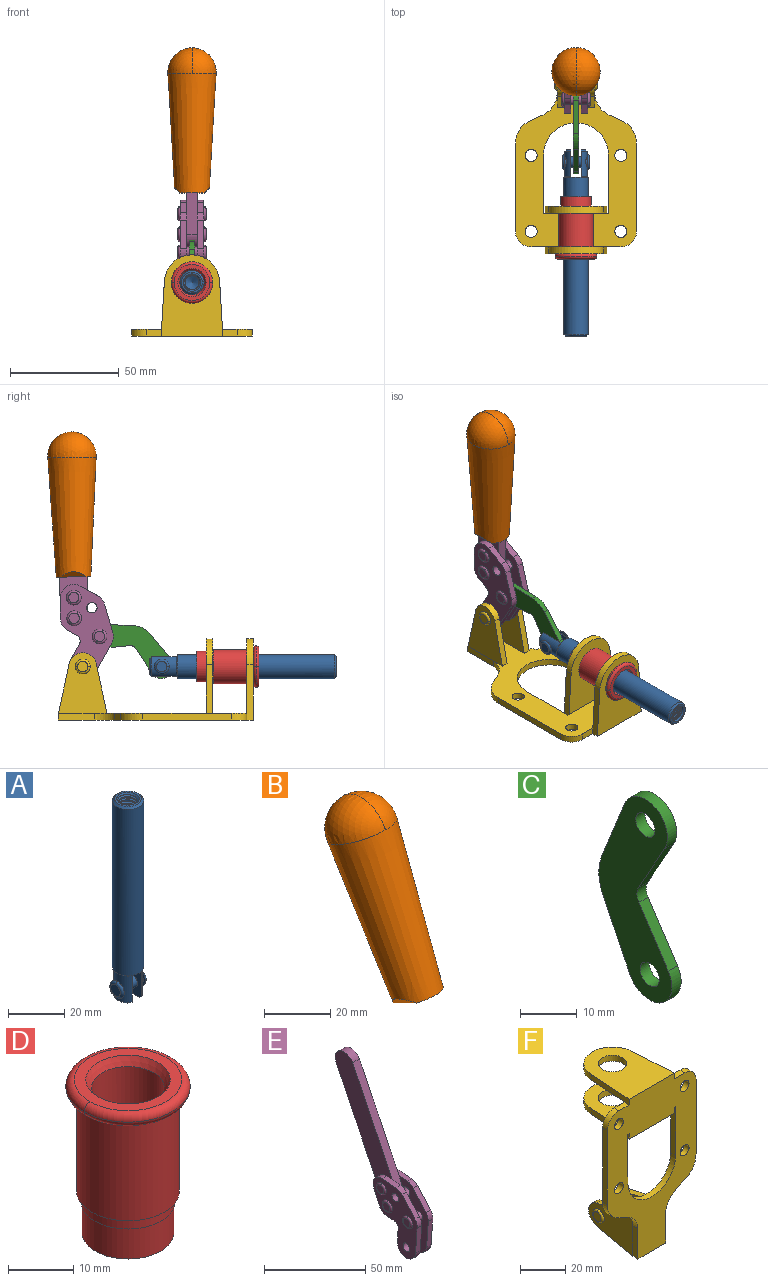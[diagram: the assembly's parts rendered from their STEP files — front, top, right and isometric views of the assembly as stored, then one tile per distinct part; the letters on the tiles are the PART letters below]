
ASSEMBLY  parts=6 mates=6
PART A: 48 faces, bbox 12.6x11.1x86.1 mm
  f0: torus R=2.41mm, axis (-1,0,0), area 15mm2, adj f30,f32,f34
  f1: torus R=2.41mm, axis (-1,0,0), area 15mm2, adj f29,f31,f33
  f2: cylinder r=5.54mm len=72.39mm, axis (0,0,1), area 2518.5mm2, adj f3,f4,f42,f43
  f3: cone r=5.54mm half-angle=45deg, axis (0,0,1), area 7.6mm2, adj f2,f5,f41
  f4: cone r=5.54mm half-angle=45deg, axis (0,0,-1), area 34.9mm2, adj f2,f39
  f5: cylinder r=5.08mm len=11.48mm, axis (0,0,1), area 108.3mm2, adj f3,f7,f8,f41
  f6: cylinder r=2.41mm len=4.83mm, axis (-1,0,0), area 71.2mm2, adj f40,f41
  f7: cylinder r=2.41mm len=4.83mm, axis (-1,0,0), area 7.6mm2, adj f5,f34
  f8: cone r=5.08mm half-angle=45deg, axis (0,0,1), area 10.6mm2, adj f5,f37,f41
  f9: cone r=3.98mm half-angle=45deg, axis (0,0,1), area 17.6mm2, adj f27,f39,f45,f46,f47
  f10: cylinder r=2.41mm len=4.83mm, axis (-1,0,0), area 7.6mm2, adj f33,f38
  f11: cylinder r=3.2mm len=6.4mm, axis (0,0,1), area 78.4mm2, adj f12,f28,f44,f45,f47
  f12: cylinder r=3.2mm len=6.4mm, axis (0,0,1), area 10.5mm2, adj f11,f13,f45,f47
  f13: cylinder r=3.2mm len=6.4mm, axis (0,0,1), area 10.5mm2, adj f12,f14,f45,f47
  f14: cylinder r=3.2mm len=6.4mm, axis (0,0,1), area 10.5mm2, adj f13,f15,f45,f47
  f15: cylinder r=3.2mm len=6.4mm, axis (0,0,1), area 10.5mm2, adj f14,f16,f45,f47
  f16: cylinder r=3.2mm len=6.4mm, axis (0,0,1), area 10.5mm2, adj f15,f17,f45,f47
  f17: cylinder r=3.2mm len=6.4mm, axis (0,0,1), area 10.5mm2, adj f16,f18,f45,f47
  f18: cylinder r=3.2mm len=6.4mm, axis (0,0,1), area 10.5mm2, adj f17,f19,f45,f47
  f19: cylinder r=3.2mm len=6.4mm, axis (0,0,1), area 10.5mm2, adj f18,f20,f45,f47
  f20: cylinder r=3.2mm len=6.4mm, axis (0,0,1), area 10.5mm2, adj f19,f21,f45,f47
  f21: cylinder r=3.2mm len=6.4mm, axis (0,0,1), area 10.5mm2, adj f20,f22,f45,f47
  f22: cylinder r=3.2mm len=6.4mm, axis (0,0,1), area 10.5mm2, adj f21,f23,f45,f47
  f23: cylinder r=3.2mm len=6.4mm, axis (0,0,1), area 10.5mm2, adj f22,f24,f45,f47
  f24: cylinder r=3.2mm len=6.4mm, axis (0,0,1), area 10.5mm2, adj f23,f25,f45,f47
  f25: cylinder r=3.2mm len=6.4mm, axis (0,0,1), area 10.5mm2, adj f24,f26,f45,f47
  f26: cylinder r=3.2mm len=6.4mm, axis (0,0,1), area 10.5mm2, adj f25,f27,f45,f47
  f27: cylinder r=3.2mm len=6.4mm, axis (0,0,1), area 7.4mm2, adj f9,f26,f45,f47
  f28: cone r=3.2mm half-angle=60deg, axis (0,0,1), area 37.2mm2, adj f11
  f29: plane 4.83x4.83mm, normal (-1,0,0), area 18.3mm2, adj f1,f31
  f30: plane 4.83x4.83mm, normal (1,0,0), area 18.3mm2, adj f0,f32
  f31: torus R=2.41mm, axis (-1,0,0), area 15mm2, adj f1,f29,f33
  f32: torus R=2.41mm, axis (-1,0,0), area 15mm2, adj f0,f30,f34
  f33: plane 6.83x6.83mm, normal (1,0,0), area 18.3mm2, adj f1,f10,f31
  f34: plane 6.83x6.83mm, normal (-1,0,0), area 18.3mm2, adj f0,f7,f32
  f35: cone r=5.08mm half-angle=45deg, axis (0,0,1), area 10.6mm2, adj f36,f38,f40
  f36: plane 7.25x1.97mm, normal (0,0,-1), area 10mm2, adj f35,f40
  f37: plane 7.25x1.97mm, normal (0,0,-1), area 10mm2, adj f8,f41
  f38: cylinder r=5.08mm len=11.48mm, axis (0,0,1), area 108.3mm2, adj f10,f35,f40,f42
  f39: plane 9.55x9.55mm, normal (0,0,1), area 22mm2, adj f4,f9
  f40: plane 12.76x10.09mm, normal (1,0,0), area 95.7mm2, adj f6,f35,f36,f38,f42,f43
  f41: plane 12.76x10.09mm, normal (-1,0,0), area 95.7mm2, adj f3,f5,f6,f8,f37,f43
  f42: cone r=5.54mm half-angle=45deg, axis (0,0,1), area 7.6mm2, adj f2,f38,f40
  f43: plane 11.07x4.7mm, normal (0,0,-1), area 50.4mm2, adj f2,f40,f41
  f44: plane 0.89x0.62mm, normal (-1,0,0), area 0.3mm2, adj f11,f45,f46,f47
  f45: bspline ~24.8x7.63mm, area 266.6mm2, adj f9,f11,f12,f13,f14,f15,f16,f17
  f46: bspline ~24.87x7.63mm, area 73.6mm2, adj f9,f44,f45,f47
  f47: bspline ~24.98x7.63mm, area 272.5mm2, adj f9,f11,f12,f13,f14,f15,f16,f17
PART B: 11 faces, bbox 22.3x42.6x64.5 mm
  f0: sphere r=11.13mm, area 411.4mm2, adj f1,f8
  f1: cone r=11.11mm half-angle=3.3deg, axis (0,0.44,0.9), area 3251.8mm2, adj f0,f7,f8,f9,f10
  f2: cylinder r=6.16mm len=11.7mm, axis (1,0,0), area 89.5mm2, adj f3,f4,f5,f6
  f3: plane 60.23x36.75mm, normal (-1,0,0), area 763.6mm2, adj f2,f4,f6,f10
  f4: plane 51.37x25.05mm, normal (0,0.9,-0.44), area 264.2mm2, adj f2,f3,f5,f10
  f5: plane 60.23x36.75mm, normal (1,0,0), area 763.6mm2, adj f2,f4,f6,f10
  f6: plane 51.37x25.05mm, normal (0,-0.9,0.44), area 264.2mm2, adj f2,f3,f5,f10
  f7: plane 9.95x5.95mm, normal (0.71,-0.31,-0.64), area 25.8mm2, adj f1,f10
  f8: sphere r=11.13mm, area 411.4mm2, adj f0,f1
  f9: plane 9.95x5.95mm, normal (-0.71,-0.31,-0.64), area 25.8mm2, adj f1,f10
  f10: plane 14.27x11.38mm, normal (0,-0.44,-0.9), area 106.7mm2, adj f1,f3,f4,f5,f6,f7,f9
PART C: 12 faces, bbox 2.3x18.2x42.8 mm
  f0: cylinder r=2.4mm len=4.8mm, axis (1,0,0), area 34.9mm2, adj f4,f11
  f1: cylinder r=10.41mm len=8.47mm, axis (1,0,0), area 20.2mm2, adj f4,f9,f10,f11
  f2: cylinder r=3.05mm len=3.16mm, axis (1,0,0), area 7.7mm2, adj f4,f6,f7,f11
  f3: cylinder r=2.4mm len=4.8mm, axis (1,0,0), area 34.9mm2, adj f4,f11
  f4: plane 42.81x18.23mm, normal (-1,0,0), area 414.1mm2, adj f0,f1,f2,f3,f5,f6,f7,f8
  f5: cylinder r=5.54mm len=10.67mm, axis (1,0,0), area 41.8mm2, adj f4,f6,f10,f11
  f6: plane 11.66x6.53mm, normal (0,-0.87,-0.49), area 30.9mm2, adj f2,f4,f5,f11
  f7: plane 11.17x7.33mm, normal (0,-0.84,0.55), area 30.9mm2, adj f2,f4,f8,f11
  f8: cylinder r=5.54mm len=10.51mm, axis (1,0,0), area 41.8mm2, adj f4,f7,f9,f11
  f9: plane 13.67x6.67mm, normal (0,0.9,-0.44), area 35.1mm2, adj f1,f4,f8,f11
  f10: plane 14.1x5.7mm, normal (0,0.93,0.37), area 35.1mm2, adj f1,f4,f5,f11
  f11: plane 42.81x18.23mm, normal (1,0,0), area 414.1mm2, adj f0,f1,f2,f3,f5,f6,f7,f8
PART D: 15 faces, bbox 20.6x20.6x28.7 mm
  f0: torus R=8.26mm, axis (0,0,1), area 56.8mm2, adj f1,f10,f12
  f1: torus R=8.26mm, axis (0,0,1), area 56.8mm2, adj f0,f6,f13
  f2: cylinder r=5.59mm len=25.91mm, axis (0,0,1), area 909.6mm2, adj f3,f4
  f3: cone r=6.86mm half-angle=45deg, axis (0,0,-1), area 70.2mm2, adj f2,f14
  f4: cone r=6.47mm half-angle=30deg, axis (0,0,1), area 66.7mm2, adj f2,f13
  f5: cylinder r=7.04mm len=14.07mm, axis (0,0,1), area 252.6mm2, adj f11,f14
  f6: torus R=8.26mm, axis (0,0,1), area 56.8mm2, adj f1,f12,f13
  f7: cylinder r=7.16mm len=14.33mm, axis (0,0,1), area 91.5mm2, adj f9,f11
  f8: cylinder r=7.86mm len=18.42mm, axis (0,0,1), area 909.6mm2, adj f9,f10
  f9: plane 15.72x15.72mm, normal (0,0,-1), area 33mm2, adj f7,f8
  f10: plane 16.51x16.51mm, normal (0,0,-1), area 19.9mm2, adj f0,f8,f12
  f11: plane 14.33x14.33mm, normal (0,0,-1), area 5.7mm2, adj f5,f7
  f12: torus R=8.26mm, axis (0,0,1), area 56.8mm2, adj f0,f6,f10
  f13: plane 16.51x16.51mm, normal (0,0,1), area 82.7mm2, adj f1,f4,f6
  f14: plane 14.07x14.07mm, normal (0,0,-1), area 7.8mm2, adj f3,f5
PART E: 59 faces, bbox 12.9x60.2x99.6 mm
  f0: torus R=2.39mm, axis (-1,0,0), area 14.9mm2, adj f20,f43,f51
  f1: torus R=2.39mm, axis (-1,0,0), area 14.9mm2, adj f19,f42,f51
  f2: torus R=2.39mm, axis (-1,0,0), area 14.9mm2, adj f18,f35,f51
  f3: torus R=2.39mm, axis (-1,0,0), area 14.9mm2, adj f14,f17,f23
  f4: torus R=2.39mm, axis (-1,0,0), area 14.9mm2, adj f13,f16,f23
  f5: torus R=2.39mm, axis (-1,0,0), area 14.9mm2, adj f12,f15,f23
  f6: cylinder r=2.39mm len=4.78mm, axis (1,0,0), area 46.5mm2, adj f48,f50,f51
  f7: cylinder r=2.39mm len=4.78mm, axis (1,0,0), area 46.5mm2, adj f50,f51
  f8: cylinder r=6.35mm len=12.68mm, axis (1,0,0), area 61.8mm2, adj f38,f39,f50,f51
  f9: cylinder r=2.39mm len=4.78mm, axis (-1,0,0), area 70.5mm2, adj f46,f50
  f10: cylinder r=2.39mm len=4.78mm, axis (-1,0,0), area 46.5mm2, adj f23,f45,f46
  f11: cylinder r=2.39mm len=4.78mm, axis (-1,0,0), area 46.5mm2, adj f23,f46
  f12: plane 4.78x4.78mm, normal (1,0,0), area 17.9mm2, adj f5,f15
  f13: plane 4.78x4.78mm, normal (1,0,0), area 17.9mm2, adj f4,f16
  f14: plane 4.78x4.78mm, normal (1,0,0), area 17.9mm2, adj f3,f17
  f15: torus R=2.39mm, axis (-1,0,0), area 14.9mm2, adj f5,f12,f23
  f16: torus R=2.39mm, axis (-1,0,0), area 14.9mm2, adj f4,f13,f23
  f17: torus R=2.39mm, axis (-1,0,0), area 14.9mm2, adj f3,f14,f23
  f18: plane 4.78x4.78mm, normal (-1,0,0), area 17.9mm2, adj f2,f35
  f19: plane 4.78x4.78mm, normal (-1,0,0), area 17.9mm2, adj f1,f42
  f20: plane 4.78x4.78mm, normal (-1,0,0), area 17.9mm2, adj f0,f43
  f21: plane 2.26x0.2mm, normal (1,0,0), area 0.2mm2, adj f31,f44
  f22: plane 2.26x0.2mm, normal (-1,0,0), area 0.2mm2, adj f41,f44
  f23: plane 39.37x30.77mm, normal (1,0,0), area 565.5mm2, adj f3,f4,f5,f10,f11,f15,f16,f17
  f24: cylinder r=6.1mm len=4.15mm, axis (-1,0,0), area 14.7mm2, adj f23,f25,f32,f46
  f25: plane 10.25x9.01mm, normal (0,-0.75,0.66), area 42.3mm2, adj f23,f24,f26,f46
  f26: cylinder r=6.35mm len=4.64mm, axis (-1,0,0), area 15.6mm2, adj f23,f25,f27,f46
  f27: plane 15.84x3.1mm, normal (0,-1,-0.07), area 49.2mm2, adj f23,f26,f28,f46
  f28: cylinder r=6.35mm len=12.68mm, axis (-1,0,0), area 61.8mm2, adj f23,f27,f29,f46
  f29: plane 8.11x3.1mm, normal (0,1,0.07), area 25.2mm2, adj f23,f28,f30,f46
  f30: cylinder r=3.05mm len=3.25mm, axis (-1,0,0), area 14.8mm2, adj f23,f29,f31,f46
  f31: plane 5.99x3.1mm, normal (0,0.07,-1), area 18.6mm2, adj f21,f23,f30,f44,f46
  f32: plane 9.5x3.1mm, normal (0,-0.07,1), area 29.5mm2, adj f23,f24,f33,f46,f47
  f33: cylinder r=6.1mm len=8.63mm, axis (-1,0,0), area 39.1mm2, adj f23,f32,f34,f47
  f34: plane 8.65x3.96mm, normal (0,0.91,-0.42), area 29.5mm2, adj f23,f33,f44,f47
  f35: torus R=2.39mm, axis (-1,0,0), area 14.9mm2, adj f2,f18,f51
  f36: plane 10.25x9.01mm, normal (0,-0.75,0.66), area 42.3mm2, adj f37,f49,f50,f51
  f37: cylinder r=6.35mm len=4.64mm, axis (1,0,0), area 15.6mm2, adj f36,f38,f50,f51
  f38: plane 15.84x3.1mm, normal (0,-1,-0.07), area 49.2mm2, adj f8,f37,f50,f51
  f39: plane 8.11x3.1mm, normal (0,1,0.07), area 25.2mm2, adj f8,f40,f50,f51
  f40: cylinder r=3.05mm len=3.25mm, axis (1,0,0), area 14.8mm2, adj f39,f41,f50,f51
  f41: plane 5.99x3.1mm, normal (0,0.07,-1), area 18.6mm2, adj f22,f40,f44,f50,f51
  f42: torus R=2.39mm, axis (-1,0,0), area 14.9mm2, adj f1,f19,f51
  f43: torus R=2.39mm, axis (-1,0,0), area 14.9mm2, adj f0,f20,f51
  f44: cylinder r=6.35mm len=12.12mm, axis (-1,0,0), area 128.9mm2, adj f21,f22,f23,f31,f34,f41,f46,f47
  f45: plane 2.65x1.35mm, normal (1,0,0), area 1mm2, adj f10,f55
  f46: plane 39.08x20.42mm, normal (-1,0,0), area 412.5mm2, adj f9,f10,f11,f24,f25,f26,f27,f28
  f47: plane 77.62x39.82mm, normal (1,0,0), area 850mm2, adj f32,f33,f34,f44,f53,f54,f55
  f48: plane 2.65x1.35mm, normal (-1,0,0), area 1mm2, adj f6,f55
  f49: cylinder r=6.1mm len=4.15mm, axis (1,0,0), area 14.7mm2, adj f36,f50,f51,f56
  f50: plane 39.08x20.42mm, normal (1,0,0), area 412.5mm2, adj f6,f7,f8,f9,f36,f37,f38,f39
  f51: plane 39.37x30.77mm, normal (-1,0,0), area 565.5mm2, adj f0,f1,f2,f6,f7,f8,f35,f36
  f52: plane 8.65x3.96mm, normal (0,0.91,-0.42), area 29.5mm2, adj f44,f51,f57,f58
  f53: plane 68.49x33.4mm, normal (0,0.9,-0.44), area 358.1mm2, adj f44,f47,f54,f58
  f54: cylinder r=6.35mm len=12.06mm, axis (1,0,0), area 93.7mm2, adj f47,f53,f55,f58
  f55: plane 68.49x33.4mm, normal (0,-0.9,0.44), area 358.1mm2, adj f44,f45,f46,f47,f48,f50,f54,f58
  f56: plane 9.5x3.1mm, normal (0,-0.07,1), area 29.5mm2, adj f49,f50,f51,f57,f58
  f57: cylinder r=6.1mm len=8.63mm, axis (1,0,0), area 39.1mm2, adj f51,f52,f56,f58
  f58: plane 77.62x39.82mm, normal (-1,0,0), area 850mm2, adj f44,f52,f53,f54,f55,f56,f57
PART F: 55 faces, bbox 55.7x37.4x89.8 mm
  f0: torus R=2.41mm, axis (-1,0,0), area 15mm2, adj f11,f15,f25
  f1: torus R=2.41mm, axis (-1,0,0), area 15mm2, adj f10,f12,f22
  f2: cylinder r=2.78mm len=5.56mm, axis (0,-1,0), area 54.2mm2, adj f30,f54
  f3: cylinder r=14.99mm len=29.97mm, axis (0,-1,0), area 145.9mm2, adj f30,f49,f53,f54
  f4: cylinder r=2.78mm len=5.56mm, axis (0,-1,0), area 54.2mm2, adj f30,f54
  f5: cylinder r=2.78mm len=5.56mm, axis (0,-1,0), area 54.2mm2, adj f30,f54
  f6: cylinder r=2.78mm len=5.56mm, axis (0,-1,0), area 54.2mm2, adj f30,f54
  f7: cylinder r=6.35mm len=12.7mm, axis (0,0,1), area 123.6mm2, adj f27,f51
  f8: cylinder r=6.35mm len=12.7mm, axis (0,0,-1), area 124.7mm2, adj f21,f35
  f9: cylinder r=2.41mm len=11.18mm, axis (-1,0,0), area 169.4mm2, adj f16,f19
  f10: plane 4.83x4.83mm, normal (1,0,0), area 18.3mm2, adj f1,f12
  f11: plane 4.83x4.83mm, normal (-1,0,0), area 18.3mm2, adj f0,f15
  f12: torus R=2.41mm, axis (-1,0,0), area 15mm2, adj f1,f10,f22
  f13: cylinder r=6.35mm len=12.41mm, axis (1,0,0), area 53.4mm2, adj f18,f19,f22,f23
  f14: cylinder r=6.35mm len=12.41mm, axis (-1,0,0), area 53.4mm2, adj f16,f17,f24,f25
  f15: torus R=2.41mm, axis (-1,0,0), area 15mm2, adj f0,f11,f25
  f16: plane 27.86x22.35mm, normal (1,0,0), area 425.4mm2, adj f9,f14,f17,f24,f30
  f17: plane 22.86x4.97mm, normal (0,0.21,0.98), area 72.5mm2, adj f14,f16,f25,f30
  f18: plane 22.86x4.97mm, normal (0,0.21,0.98), area 72.5mm2, adj f13,f19,f22,f30
  f19: plane 27.86x22.35mm, normal (-1,0,0), area 425.4mm2, adj f9,f13,f18,f23,f30
  f20: cylinder r=12.7mm len=25.35mm, axis (0,0,-1), area 119.8mm2, adj f21,f34,f35,f36
  f21: plane 34.21x28.07mm, normal (0,0,-1), area 702.4mm2, adj f8,f20,f30,f34,f36
  f22: plane 27.96x22.45mm, normal (1,0,0), area 407.2mm2, adj f1,f12,f13,f18,f23,f30,f42,f43
  f23: plane 22.86x4.97mm, normal (0,0.21,-0.98), area 72.5mm2, adj f13,f19,f22,f44
  f24: plane 22.86x4.97mm, normal (0,0.21,-0.98), area 72.5mm2, adj f14,f16,f25,f44
  f25: plane 27.86x22.35mm, normal (-1,0,0), area 407.1mm2, adj f0,f14,f15,f17,f24,f30,f45,f46
  f26: plane 3.1x0.95mm, normal (0,0,-1), area 2.7mm2, adj f30,f49,f50,f54
  f27: plane 34.21x28.07mm, normal (0,0,1), area 702.4mm2, adj f7,f28,f30,f50,f52
  f28: cylinder r=12.7mm len=25.35mm, axis (0,0,1), area 118.8mm2, adj f27,f50,f51,f52
  f29: plane 3.1x0.95mm, normal (0,0,-1), area 2.7mm2, adj f30,f52,f53,f54
  f30: plane 86.54x55.63mm, normal (0,1,0), area 2362.9mm2, adj f2,f3,f4,f5,f6,f16,f17,f18
  f31: plane 40.56x3.1mm, normal (-1,0,0), area 125.7mm2, adj f30,f32,f48,f54
  f32: cylinder r=7.11mm len=7.11mm, axis (0,-1,0), area 34.6mm2, adj f30,f31,f33,f54
  f33: plane 6.67x3.1mm, normal (0,0,1), area 20.4mm2, adj f30,f32,f34,f54
  f34: plane 25.39x3.13mm, normal (-1,0.06,0), area 79.5mm2, adj f20,f21,f33,f35,f54
  f35: plane 37.31x28.45mm, normal (0,0,1), area 789.9mm2, adj f8,f20,f34,f36,f54
  f36: plane 25.39x3.13mm, normal (1,0.06,0), area 79.5mm2, adj f20,f21,f35,f37,f54
  f37: plane 6.67x3.1mm, normal (0,0,1), area 20.4mm2, adj f30,f36,f38,f54
  f38: cylinder r=7.11mm len=7.11mm, axis (0,-1,0), area 34.6mm2, adj f30,f37,f39,f54
  f39: plane 40.56x3.1mm, normal (1,0,0), area 125.7mm2, adj f30,f38,f40,f54
  f40: cylinder r=11.18mm len=10.16mm, axis (0,-1,0), area 39.5mm2, adj f30,f39,f41,f54
  f41: plane 6.09x3.1mm, normal (0.42,0,-0.91), area 20.8mm2, adj f30,f40,f42,f54
  f42: cylinder r=11.18mm len=9.41mm, axis (0,-1,0), area 37.2mm2, adj f22,f30,f41,f43,f54
  f43: plane 16.5x3.1mm, normal (1,0,0), area 51.1mm2, adj f22,f42,f44,f54
  f44: plane 17.37x3.1mm, normal (0,0,-1), area 53.8mm2, adj f23,f24,f30,f43,f45,f54
  f45: plane 16.5x3.1mm, normal (-1,0,0), area 51.1mm2, adj f25,f44,f46,f54
  f46: cylinder r=11.18mm len=9.41mm, axis (0,-1,0), area 37.2mm2, adj f25,f30,f45,f47,f54
  f47: plane 6.09x3.1mm, normal (-0.42,0,-0.91), area 20.8mm2, adj f30,f46,f48,f54
  f48: cylinder r=11.18mm len=10.16mm, axis (0,-1,0), area 39.5mm2, adj f30,f31,f47,f54
  f49: plane 26.54x3.1mm, normal (-1,0,0), area 82.3mm2, adj f3,f26,f30,f54
  f50: plane 25.39x3.1mm, normal (1,0.06,0), area 78.8mm2, adj f26,f27,f28,f51,f54
  f51: plane 37.31x28.45mm, normal (0,0,-1), area 789.9mm2, adj f7,f28,f50,f52,f54
  f52: plane 25.39x3.1mm, normal (-1,0.06,0), area 78.8mm2, adj f27,f28,f29,f51,f54
  f53: plane 26.54x3.1mm, normal (1,0,0), area 82.3mm2, adj f3,f29,f30,f54
  f54: plane 89.66x55.63mm, normal (0,-1,0), area 2678.5mm2, adj f2,f3,f4,f5,f6,f26,f29,f31
PLACE A rot(axis=(1,0,0),90deg) t=(0,12.48,0)mm
PLACE B rot(axis=(1,0,0),25.2deg) t=(0,-2.62,43.16)mm
PLACE C rot(axis=(1,0,0),117.9deg) t=(0,22.19,10.09)mm
PLACE D rot(axis=(1,0,0),90deg) t=(0,1.23,0)mm
PLACE E rot(axis=(1,0,0),25.2deg) t=(0,-2.62,43.16)mm
PLACE F rot(axis=(1,0,0),90deg) t=(0,1.23,0)mm fixed
MATE revolute C.f3 <-> E.f4  axis (1,0,0) through (0,25.57,38.47)mm
MATE revolute A.f6 <-> C.f5  axis (-1,0,0) through (0,-2.99,24.61)mm
MATE slider A.f2 <-> F.f7  axis (0,-1,0) through (0,-46.3,24.61)mm
MATE fastened E.f54 <-> B.f2  axis (1,0,0) through (0,38.31,122.98)mm
MATE revolute E.f7 <-> F.f0  axis (1,0,0) through (0,33.32,24.61)mm
MATE fastened D.f0 <-> F.f7  axis (0,1,0) through (0,-45.16,24.61)mm
